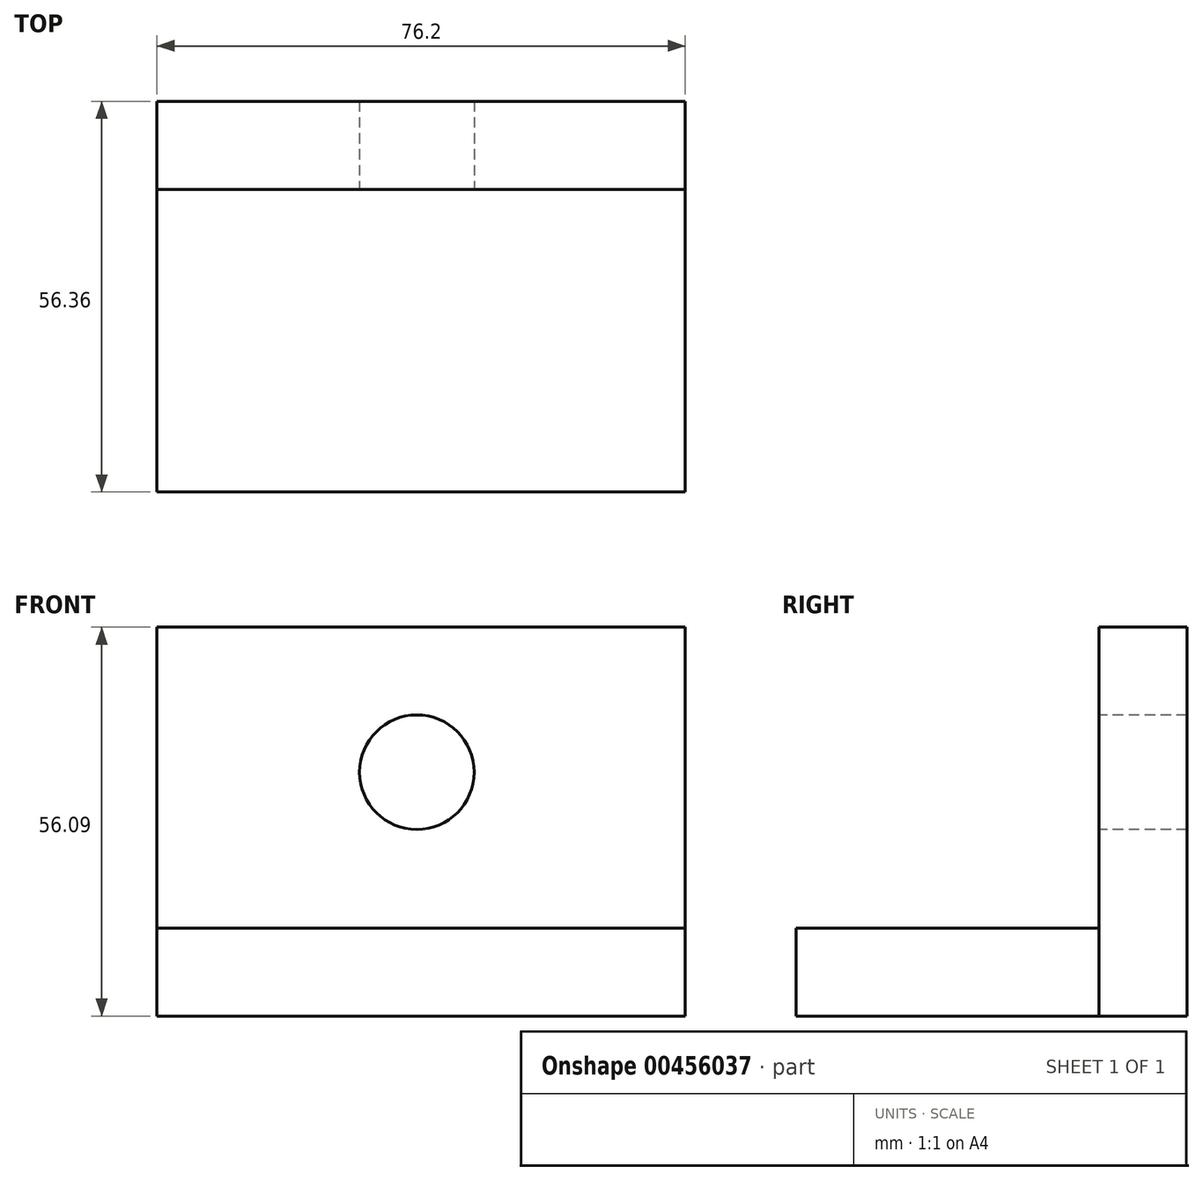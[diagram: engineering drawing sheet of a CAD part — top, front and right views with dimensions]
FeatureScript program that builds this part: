
annotation { "Feature Type Name" : "Feature", "Feature Type Description" : "" }
export const myFeature = defineFeature(function(context is Context, id is Id, definition is map)
    precondition{}
    {
        {
            var Q0;
            Q0=qCreatedBy(makeId("Right.planeOp"),FACE);
            var sketch = newSketch(context, id + "F0", { "sketchPlane" : qUnion([Q0])});
            skLineSegment(sketch, "E0.bottom", {"start": v(0, 0) * mm, "end": v(-12.7, 0) * mm});
            skLineSegment(sketch, "E0.top", {"start": v(0, 56.1) * mm, "end": v(-12.7, 56.1) * mm});
            skLineSegment(sketch, "E0.left", {"start": v(0, 0) * mm, "end": v(0, 56.1) * mm});
            skLineSegment(sketch, "E0.right", {"start": v(-12.7, 0) * mm, "end": v(-12.7, 56.1) * mm});
            skSolve(sketch);
        }
        {
            var Q0;
            Q0=makeQuery(id+"F0.imprint","IMPRINT",FACE,{"disambiguationData":[TD([[makeQuery(id+"F0.imprint","IMPRINT",EDGE,{"derivedFrom":sQuery(id+"F0.wireOp",EDGE,"E0.bottom")}),-1.0]])]});
            extrude(context, id + "F1", {"entities" : qUnion([Q0]), "depth" : 76.2 * mm});
        }
        {
            var Q0;
            Q0=qCreatedBy(makeId("Top.planeOp"),FACE);
            var sketch = newSketch(context, id + "F2", { "sketchPlane" : qUnion([Q0])});
            skLineSegment(sketch, "E1.bottom", {"start": v(0, 0) * mm, "end": v(76.17, 0) * mm});
            skLineSegment(sketch, "E1.top", {"start": v(0, -56.36) * mm, "end": v(76.17, -56.36) * mm});
            skLineSegment(sketch, "E1.left", {"start": v(0, 0) * mm, "end": v(0, -56.36) * mm});
            skLineSegment(sketch, "E1.right", {"start": v(76.17, 0) * mm, "end": v(76.17, -56.36) * mm});
            skSolve(sketch);
        }
        {
            var Q0;
            Q0=makeQuery(id+"F2.imprint","IMPRINT",FACE,{"disambiguationData":[TD([[makeQuery(id+"F2.imprint","IMPRINT",EDGE,{"derivedFrom":sQuery(id+"F2.wireOp",EDGE,"E1.bottom")}),-1.0]])]});
            extrude(context, id + "F3", {"entities" : qUnion([Q0]), "operationType" : NewBodyOperationType.ADD, "depth" : 12.7 * mm});
        }
        {
            var Q0;
            Q0=makeQuery(id+"F1.opExtrude","SWEPT_FACE",FACE,{"disambiguationData":[OSD([sQuery(id+"F0.wireOp",EDGE,"E0.right")])]});
            var sketch = newSketch(context, id + "F4", { "sketchPlane" : qUnion([Q0])});
            skCircle(sketch, "E2", {"center": v(37.47, 35.17) * mm, "radius": 8.26 * mm});
            skSolve(sketch);
        }
        {
            var Q0;
            Q0=makeQuery(id+"F4.imprint","IMPRINT",FACE,{"disambiguationData":[TD([[makeQuery(id+"F4.imprint","IMPRINT",EDGE,{"derivedFrom":sQuery(id+"F4.wireOp",EDGE,"E2")}),1.0]])]});
            extrude(context, id + "F5", {"entities" : qUnion([Q0]), "operationType" : NewBodyOperationType.REMOVE, "oppositeDirection" : true, "depth" : 25.4 * mm});
        }
    });
